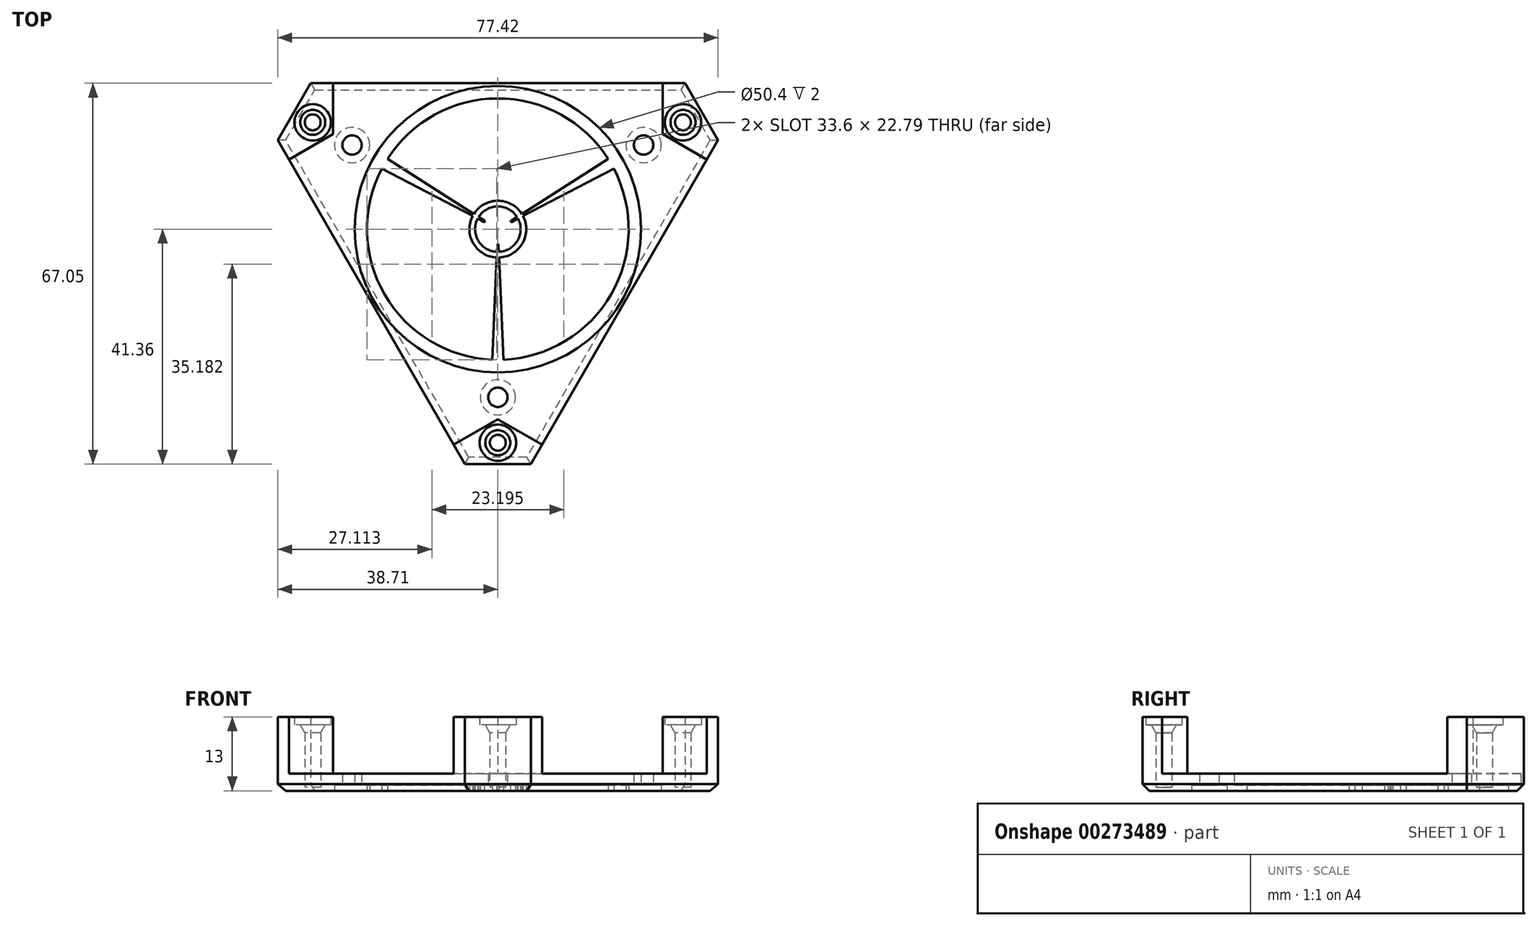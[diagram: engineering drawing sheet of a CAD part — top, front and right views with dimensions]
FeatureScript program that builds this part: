
annotation { "Feature Type Name" : "Feature", "Feature Type Description" : "" }
export const myFeature = defineFeature(function(context is Context, id is Id, definition is map)
    precondition{}
    {
        {
            var Q0;
            Q0=qCreatedBy(makeId("Top.planeOp"),FACE);
            var sketch = newSketch(context, id + "F0", { "sketchPlane" : qUnion([Q0])});
            skLineSegment(sketch, "E0", {"start": v(0, 0) * mm, "end": v(0, 47) * mm, "construction": true});
            skLineSegment(sketch, "E1", {"start": v(0, 47) * mm, "end": v(15, 47) * mm, "construction": true});
            skLineSegment(sketch, "E2", {"start": v(0, 0) * mm, "end": v(0, -29.6) * mm, "construction": true});
            skCircle(sketch, "E3", {"center": v(0, -29.6) * mm, "radius": 1.7 * mm});
            skCircle(sketch, "E4", {"center": v(15, 47) * mm, "radius": 1.7 * mm});
            skLineSegment(sketch, "E5", {"start": v(13.3, 47) * mm, "end": v(13.3, 49.47) * mm});
            skLineSegment(sketch, "E6", {"start": v(13.3, 47) * mm, "end": v(13.3, 44.53) * mm});
            skCircle(sketch, "E7", {"center": v(0, -29.6) * mm, "radius": 3.1 * mm});
            skCircle(sketch, "E8", {"center": v(0, 0) * mm, "radius": 4 * mm});
            skCircle(sketch, "E9", {"center": v(0, 0) * mm, "radius": 25.2 * mm});
            skCircle(sketch, "E10", {"center": v(0, 0) * mm, "radius": 23 * mm});
            skCircle(sketch, "E11", {"center": v(0, 0) * mm, "radius": 5 * mm});
            skLineSegment(sketch, "E12", {"start": v(0, -29.6) * mm, "end": v(0, -33.6) * mm, "construction": true});
            skLineSegment(sketch, "E13", {"start": v(0, -33.6) * mm, "end": v(0, 55) * mm, "construction": true});
            skLineSegment(sketch, "E14", {"start": v(0, 55) * mm, "end": v(11, 55) * mm});
            skLineSegment(sketch, "E15.5.0", {"start": v(0, 0) * mm, "end": v(28.5, 16.45) * mm, "construction": true});
            skLineSegment(sketch, "E16", {"start": v(11, 55) * mm, "end": v(28.5, 40.45) * mm});
            skCircle(sketch, "E17", {"center": v(15, 47) * mm, "radius": 3 * mm});
            skLineSegment(sketch, "E18", {"start": v(13.3, 49.47) * mm, "end": v(13.3, 44.53) * mm});
            skCircle(sketch, "E19", {"center": v(0, 0) * mm, "radius": 0.5 * mm});
            skLineSegment(sketch, "E20", {"start": v(0, -0.5) * mm, "end": v(1, -22.98) * mm});
            skLineSegment(sketch, "E21.MirrorCS", {"start": v(0, -0.5) * mm, "end": v(-1, -22.98) * mm});
            skLineSegment(sketch, "E22", {"start": v(28.5, 40.45) * mm, "end": v(28.5, 16.45) * mm});
            skLineSegment(sketch, "E23.MirrorCS", {"start": v(-13.3, 49.47) * mm, "end": v(-13.3, 44.53) * mm});
            skLineSegment(sketch, "E24.MirrorCS", {"start": v(0, 55) * mm, "end": v(-11, 55) * mm});
            skCircle(sketch, "E25.MirrorC", {"center": v(-15, 47) * mm, "radius": 1.7 * mm});
            skCircle(sketch, "E26.MirrorC", {"center": v(-15, 47) * mm, "radius": 3 * mm});
            skLineSegment(sketch, "E27.MirrorCS", {"start": v(-28.5, 40.45) * mm, "end": v(-28.5, 16.45) * mm});
            skLineSegment(sketch, "E28.MirrorCS", {"start": v(-11, 55) * mm, "end": v(-28.5, 40.45) * mm});
            skLineSegment(sketch, "E29.1.0", {"start": v(-42.13, -37.03) * mm, "end": v(-20.78, -44.9) * mm});
            skLineSegment(sketch, "E29.1.1", {"start": v(-36.2, -36.25) * mm, "end": v(-31.91, -33.78) * mm});
            skLineSegment(sketch, "E29.1.2", {"start": v(-47.63, -27.5) * mm, "end": v(-42.13, -37.03) * mm});
            skLineSegment(sketch, "E29.1.3", {"start": v(-20.78, -44.9) * mm, "end": v(0, -32.9) * mm});
            skCircle(sketch, "E29.1.4", {"center": v(-33.2, -36.5) * mm, "radius": 1.7 * mm});
            skCircle(sketch, "E29.1.5", {"center": v(-33.2, -36.5) * mm, "radius": 3 * mm});
            skLineSegment(sketch, "E29.1.6", {"start": v(-47.63, -27.5) * mm, "end": v(-53.13, -17.97) * mm});
            skLineSegment(sketch, "E29.1.7", {"start": v(-53.13, -17.97) * mm, "end": v(-49.28, 4.45) * mm});
            skLineSegment(sketch, "E29.1.8", {"start": v(-49.28, 4.45) * mm, "end": v(-28.5, 16.45) * mm});
            skCircle(sketch, "E29.1.9", {"center": v(-48.2, -10.5) * mm, "radius": 3 * mm});
            skLineSegment(sketch, "E29.1.10", {"start": v(-49.5, -13.22) * mm, "end": v(-45.21, -10.75) * mm});
            skCircle(sketch, "E29.1.11", {"center": v(-48.2, -10.5) * mm, "radius": 1.7 * mm});
            skLineSegment(sketch, "E29.1.12", {"start": v(0.43, 0.25) * mm, "end": v(19.4, 12.36) * mm});
            skLineSegment(sketch, "E29.1.13", {"start": v(0.43, 0.25) * mm, "end": v(20.4, 10.62) * mm});
            skCircle(sketch, "E29.1.14", {"center": v(25.63, 14.8) * mm, "radius": 3.1 * mm});
            skCircle(sketch, "E29.1.15", {"center": v(25.63, 14.8) * mm, "radius": 1.7 * mm});
            skLineSegment(sketch, "E29.2.0", {"start": v(53.13, -17.97) * mm, "end": v(49.28, 4.45) * mm});
            skLineSegment(sketch, "E29.2.1", {"start": v(49.5, -13.22) * mm, "end": v(45.21, -10.75) * mm});
            skLineSegment(sketch, "E29.2.2", {"start": v(47.63, -27.5) * mm, "end": v(53.13, -17.97) * mm});
            skLineSegment(sketch, "E29.2.3", {"start": v(49.28, 4.45) * mm, "end": v(28.5, 16.45) * mm});
            skCircle(sketch, "E29.2.4", {"center": v(48.2, -10.5) * mm, "radius": 1.7 * mm});
            skCircle(sketch, "E29.2.5", {"center": v(48.2, -10.5) * mm, "radius": 3 * mm});
            skLineSegment(sketch, "E29.2.6", {"start": v(47.63, -27.5) * mm, "end": v(42.13, -37.03) * mm});
            skLineSegment(sketch, "E29.2.7", {"start": v(42.13, -37.03) * mm, "end": v(20.78, -44.9) * mm});
            skLineSegment(sketch, "E29.2.8", {"start": v(20.78, -44.9) * mm, "end": v(0, -32.9) * mm});
            skCircle(sketch, "E29.2.9", {"center": v(33.2, -36.5) * mm, "radius": 3 * mm});
            skLineSegment(sketch, "E29.2.10", {"start": v(36.2, -36.25) * mm, "end": v(31.91, -33.78) * mm});
            skCircle(sketch, "E29.2.11", {"center": v(33.2, -36.5) * mm, "radius": 1.7 * mm});
            skLineSegment(sketch, "E29.2.12", {"start": v(-0.43, 0.25) * mm, "end": v(-20.4, 10.62) * mm});
            skLineSegment(sketch, "E29.2.13", {"start": v(-0.43, 0.25) * mm, "end": v(-19.4, 12.36) * mm});
            skCircle(sketch, "E29.2.14", {"center": v(-25.63, 14.8) * mm, "radius": 3.1 * mm});
            skCircle(sketch, "E29.2.15", {"center": v(-25.63, 14.8) * mm, "radius": 1.7 * mm});
            skLineSegment(sketch, "E30", {"start": v(0, -29.6) * mm, "end": v(0, -37.6) * mm, "construction": true});
            skCircle(sketch, "E31", {"center": v(0, -37.6) * mm, "radius": 1.4 * mm});
            skCircle(sketch, "E32", {"center": v(0, -37.6) * mm, "radius": 3.2 * mm});
            skLineSegment(sketch, "E33", {"start": v(8, -37.53) * mm, "end": v(5.8, -41.36) * mm});
            skLineSegment(sketch, "E34", {"start": v(5.8, -41.36) * mm, "end": v(5.8, -41.36) * mm});
            skLineSegment(sketch, "E35.MirrorCS", {"start": v(-8, -37.53) * mm, "end": v(-5.8, -41.36) * mm});
            skLineSegment(sketch, "E36", {"start": v(-5.8, -41.36) * mm, "end": v(5.8, -41.36) * mm});
            skLineSegment(sketch, "E37.1.0", {"start": v(28.5, 25.7) * mm, "end": v(32.92, 25.7) * mm});
            skLineSegment(sketch, "E37.1.1", {"start": v(38.7, 15.66) * mm, "end": v(32.92, 25.7) * mm});
            skLineSegment(sketch, "E37.1.2", {"start": v(36.5, 11.84) * mm, "end": v(38.7, 15.66) * mm});
            skCircle(sketch, "E37.1.3", {"center": v(32.56, 18.8) * mm, "radius": 3.2 * mm});
            skCircle(sketch, "E37.1.4", {"center": v(32.56, 18.8) * mm, "radius": 1.4 * mm});
            skLineSegment(sketch, "E37.2.0", {"start": v(-36.5, 11.84) * mm, "end": v(-38.7, 15.66) * mm});
            skLineSegment(sketch, "E37.2.1", {"start": v(-32.92, 25.7) * mm, "end": v(-38.7, 15.66) * mm});
            skLineSegment(sketch, "E37.2.2", {"start": v(-28.5, 25.7) * mm, "end": v(-32.92, 25.7) * mm});
            skCircle(sketch, "E37.2.3", {"center": v(-32.56, 18.8) * mm, "radius": 3.2 * mm});
            skCircle(sketch, "E37.2.4", {"center": v(-32.56, 18.8) * mm, "radius": 1.4 * mm});
            skLineSegment(sketch, "E38", {"start": v(8, -37.53) * mm, "end": v(36.5, 11.84) * mm});
            skLineSegment(sketch, "E39", {"start": v(-8, -37.53) * mm, "end": v(-36.5, 11.84) * mm});
            skLineSegment(sketch, "E40", {"start": v(-28.5, 25.7) * mm, "end": v(28.5, 25.7) * mm});
            skLineSegment(sketch, "E41", {"start": v(-7.76, -37.95) * mm, "end": v(0, -33.47) * mm});
            skLineSegment(sketch, "E42", {"start": v(0, -33.47) * mm, "end": v(7.76, -37.95) * mm});
            skLineSegment(sketch, "E43.1.0", {"start": v(36.74, 12.25) * mm, "end": v(28.98, 16.73) * mm});
            skLineSegment(sketch, "E43.1.1", {"start": v(28.98, 16.73) * mm, "end": v(28.98, 25.7) * mm});
            skLineSegment(sketch, "E43.2.0", {"start": v(-28.98, 25.7) * mm, "end": v(-28.98, 16.73) * mm});
            skLineSegment(sketch, "E43.2.1", {"start": v(-28.98, 16.73) * mm, "end": v(-36.74, 12.25) * mm});
            skSolve(sketch);
        }
        {
            var Q0;
            Q0=makeQuery(id+"F0.imprint","IMPRINT",FACE,{"disambiguationData":[TD([[makeQuery(id+"F0.imprint","IMPRINT",EDGE,{"derivedFrom":sQuery(id+"F0.wireOp",EDGE,"E7")}),-1.0]])]});
            var Q1;
            Q1=makeQuery(id+"F0.imprint","IMPRINT",FACE,{"disambiguationData":[TD([[makeQuery(id+"F0.imprint","IMPRINT",EDGE,{"derivedFrom":sQuery(id+"F0.wireOp",EDGE,"E29.2.14")}),1.0]])]});
            var Q2;
            Q2=makeQuery(id+"F0.imprint","IMPRINT",FACE,{"disambiguationData":[TD([[makeQuery(id+"F0.imprint","IMPRINT",EDGE,{"derivedFrom":sQuery(id+"F0.wireOp",EDGE,"E29.1.14")}),1.0]])]});
            var Q3;
            Q3=makeQuery(id+"F0.imprint","IMPRINT",FACE,{"disambiguationData":[TD([[makeQuery(id+"F0.imprint","IMPRINT",EDGE,{"derivedFrom":sQuery(id+"F0.wireOp",EDGE,"E3")}),-1.0]])]});
            var Q4;
            {var subQ3=sQuery(id+"F0.wireOp",EDGE,"E43.2.0");Q4=makeQuery(id+"F0.imprint","IMPRINT",FACE,{"disambiguationData":[TD([[makeQuery(id+"F0.imprint","IMPRINT",EDGE,{"derivedFrom":subQ3}),1.0]])]});}
            var Q5;
            {var subQ3=sQuery(id+"F0.wireOp",EDGE,"E43.1.0");Q5=makeQuery(id+"F0.imprint","IMPRINT",FACE,{"disambiguationData":[TD([[makeQuery(id+"F0.imprint","IMPRINT",EDGE,{"derivedFrom":subQ3}),1.0]])]});}
            var Q6;
            {var subQ3=sQuery(id+"F0.wireOp",EDGE,"E41");Q6=makeQuery(id+"F0.imprint","IMPRINT",FACE,{"disambiguationData":[TD([[makeQuery(id+"F0.imprint","IMPRINT",EDGE,{"derivedFrom":subQ3}),1.0]])]});}
            extrude(context, id + "F1", {"entities" : qUnion([Q0, Q1, Q2, Q3, Q4, Q5, Q6]), "offsetDistance" : 25 * mm, "depth" : 3 * mm});
        }
        {
            var Q0;
            {var subQ0=sQuery(id+"F0.wireOp",EDGE,"E20");var subQ1=sQuery(id+"F0.wireOp",EDGE,"E10");var subQ2=makeQuery(id+"F0.imprint","INTERSECT",VERTEX,{"derivedFrom":[subQ1,subQ0]});Q0=makeQuery(id+"F0.imprint","IMPRINT",FACE,{"disambiguationData":[TD([[makeQuery(id+"F0.imprint","IMPRINT",EDGE,{"disambiguationData":[TD([[subQ2,1.0]])],"derivedFrom":subQ1}),1.0]])]});}
            var Q1;
            Q1=makeQuery(id+"F0.imprint","IMPRINT",FACE,{"disambiguationData":[TD([[makeQuery(id+"F0.imprint","IMPRINT",EDGE,{"derivedFrom":sQuery(id+"F0.wireOp",EDGE,"E9")}),1.0]])]});
            var Q2;
            {var subQ0=sQuery(id+"F0.wireOp",EDGE,"E29.1.12");var subQ1=sQuery(id+"F0.wireOp",EDGE,"E10");var subQ2=makeQuery(id+"F0.imprint","INTERSECT",VERTEX,{"derivedFrom":[subQ1,subQ0]});Q2=makeQuery(id+"F0.imprint","IMPRINT",FACE,{"disambiguationData":[TD([[makeQuery(id+"F0.imprint","IMPRINT",EDGE,{"disambiguationData":[TD([[subQ2,1.0]])],"derivedFrom":subQ1}),1.0]])]});}
            var Q3;
            {var subQ0=sQuery(id+"F0.wireOp",EDGE,"E29.2.12");var subQ1=sQuery(id+"F0.wireOp",EDGE,"E10");var subQ2=makeQuery(id+"F0.imprint","INTERSECT",VERTEX,{"derivedFrom":[subQ1,subQ0]});Q3=makeQuery(id+"F0.imprint","IMPRINT",FACE,{"disambiguationData":[TD([[makeQuery(id+"F0.imprint","IMPRINT",EDGE,{"disambiguationData":[TD([[subQ2,1.0]])],"derivedFrom":subQ1}),1.0]])]});}
            var Q4;
            {var subQ0=sQuery(id+"F0.wireOp",EDGE,"E29.2.12");var subQ1=sQuery(id+"F0.wireOp",EDGE,"E8");var subQ2=makeQuery(id+"F0.imprint","INTERSECT",VERTEX,{"derivedFrom":[subQ1,subQ0]});Q4=makeQuery(id+"F0.imprint","IMPRINT",FACE,{"disambiguationData":[TD([[makeQuery(id+"F0.imprint","IMPRINT",EDGE,{"disambiguationData":[TD([[subQ2,-1.0]])],"derivedFrom":subQ1}),-1.0]])]});}
            var Q5;
            {var subQ0=sQuery(id+"F0.wireOp",EDGE,"E29.1.13");var subQ1=sQuery(id+"F0.wireOp",EDGE,"E8");var subQ2=makeQuery(id+"F0.imprint","INTERSECT",VERTEX,{"derivedFrom":[subQ1,subQ0]});Q5=makeQuery(id+"F0.imprint","IMPRINT",FACE,{"disambiguationData":[TD([[makeQuery(id+"F0.imprint","IMPRINT",EDGE,{"disambiguationData":[TD([[subQ2,1.0]])],"derivedFrom":subQ1}),-1.0]])]});}
            var Q6;
            {var subQ0=sQuery(id+"F0.wireOp",EDGE,"E21.MirrorCS");var subQ1=sQuery(id+"F0.wireOp",EDGE,"E8");var subQ2=makeQuery(id+"F0.imprint","INTERSECT",VERTEX,{"derivedFrom":[subQ1,subQ0]});Q6=makeQuery(id+"F0.imprint","IMPRINT",FACE,{"disambiguationData":[TD([[makeQuery(id+"F0.imprint","IMPRINT",EDGE,{"disambiguationData":[TD([[subQ2,-1.0]])],"derivedFrom":subQ1}),-1.0]])]});}
            var Q7;
            {var subQ0=sQuery(id+"F0.wireOp",EDGE,"E29.1.12");var subQ1=sQuery(id+"F0.wireOp",EDGE,"E8");var subQ2=makeQuery(id+"F0.imprint","INTERSECT",VERTEX,{"derivedFrom":[subQ1,subQ0]});Q7=makeQuery(id+"F0.imprint","IMPRINT",FACE,{"disambiguationData":[TD([[makeQuery(id+"F0.imprint","IMPRINT",EDGE,{"disambiguationData":[TD([[subQ2,1.0]])],"derivedFrom":subQ1}),-1.0]])]});}
            var Q8;
            {var subQ0=sQuery(id+"F0.wireOp",EDGE,"E29.1.12");var subQ1=sQuery(id+"F0.wireOp",EDGE,"E8");var subQ2=makeQuery(id+"F0.imprint","INTERSECT",VERTEX,{"derivedFrom":[subQ1,subQ0]});Q8=makeQuery(id+"F0.imprint","IMPRINT",FACE,{"disambiguationData":[TD([[makeQuery(id+"F0.imprint","IMPRINT",EDGE,{"disambiguationData":[TD([[subQ2,-1.0]])],"derivedFrom":subQ1}),-1.0]])]});}
            var Q9;
            {var subQ0=sQuery(id+"F0.wireOp",EDGE,"E29.2.13");var subQ1=sQuery(id+"F0.wireOp",EDGE,"E8");var subQ2=makeQuery(id+"F0.imprint","INTERSECT",VERTEX,{"derivedFrom":[subQ1,subQ0]});Q9=makeQuery(id+"F0.imprint","IMPRINT",FACE,{"disambiguationData":[TD([[makeQuery(id+"F0.imprint","IMPRINT",EDGE,{"disambiguationData":[TD([[subQ2,-1.0]])],"derivedFrom":subQ1}),-1.0]])]});}
            var Q10;
            {var subQ0=sQuery(id+"F0.wireOp",EDGE,"E29.1.12");var subQ1=sQuery(id+"F0.wireOp",EDGE,"E8");var subQ2=makeQuery(id+"F0.imprint","INTERSECT",VERTEX,{"derivedFrom":[subQ1,subQ0]});Q10=makeQuery(id+"F0.imprint","IMPRINT",FACE,{"disambiguationData":[TD([[makeQuery(id+"F0.imprint","IMPRINT",EDGE,{"disambiguationData":[TD([[subQ2,1.0]])],"derivedFrom":subQ1}),1.0]])]});}
            var Q11;
            {var subQ0=sQuery(id+"F0.wireOp",EDGE,"E29.2.13");var subQ1=sQuery(id+"F0.wireOp",EDGE,"E8");var subQ2=makeQuery(id+"F0.imprint","INTERSECT",VERTEX,{"derivedFrom":[subQ1,subQ0]});Q11=makeQuery(id+"F0.imprint","IMPRINT",FACE,{"disambiguationData":[TD([[makeQuery(id+"F0.imprint","IMPRINT",EDGE,{"disambiguationData":[TD([[subQ2,-1.0]])],"derivedFrom":subQ1}),1.0]])]});}
            var Q12;
            {var subQ0=sQuery(id+"F0.wireOp",EDGE,"E21.MirrorCS");var subQ1=sQuery(id+"F0.wireOp",EDGE,"E8");var subQ2=makeQuery(id+"F0.imprint","INTERSECT",VERTEX,{"derivedFrom":[subQ1,subQ0]});Q12=makeQuery(id+"F0.imprint","IMPRINT",FACE,{"disambiguationData":[TD([[makeQuery(id+"F0.imprint","IMPRINT",EDGE,{"disambiguationData":[TD([[subQ2,-1.0]])],"derivedFrom":subQ1}),1.0]])]});}
            extrude(context, id + "F2", {"entities" : qUnion([Q0, Q1, Q2, Q3, Q4, Q5, Q6, Q7, Q8, Q9, Q10, Q11, Q12]), "operationType" : NewBodyOperationType.ADD, "depth" : 1 * mm});
        }
        {
            var Q0;
            {var subQ1=sQuery(id+"F0.wireOp",EDGE,"E37.2.1");Q0=makeQuery(id+"F0.imprint","IMPRINT",FACE,{"disambiguationData":[TD([[makeQuery(id+"F0.imprint","IMPRINT",EDGE,{"derivedFrom":subQ1}),1.0]])]});}
            var Q1;
            Q1=makeQuery(id+"F0.imprint","IMPRINT",FACE,{"disambiguationData":[TD([[makeQuery(id+"F0.imprint","IMPRINT",EDGE,{"derivedFrom":sQuery(id+"F0.wireOp",EDGE,"E32")}),-1.0]])]});
            var Q2;
            {var subQ1=sQuery(id+"F0.wireOp",EDGE,"E37.1.1");Q2=makeQuery(id+"F0.imprint","IMPRINT",FACE,{"disambiguationData":[TD([[makeQuery(id+"F0.imprint","IMPRINT",EDGE,{"derivedFrom":subQ1}),1.0]])]});}
            extrude(context, id + "F3", {"entities" : qUnion([Q0, Q1, Q2]), "operationType" : NewBodyOperationType.ADD, "depth" : (3 + 10) * mm});
        }
        {
            var Q0;
            Q0=makeQuery(id+"F0.imprint","IMPRINT",FACE,{"disambiguationData":[TD([[makeQuery(id+"F0.imprint","IMPRINT",EDGE,{"derivedFrom":sQuery(id+"F0.wireOp",EDGE,"E31")}),-1.0]])]});
            var Q1;
            Q1=makeQuery(id+"F0.imprint","IMPRINT",FACE,{"disambiguationData":[TD([[makeQuery(id+"F0.imprint","IMPRINT",EDGE,{"derivedFrom":sQuery(id+"F0.wireOp",EDGE,"E37.2.3")}),1.0]])]});
            var Q2;
            Q2=makeQuery(id+"F0.imprint","IMPRINT",FACE,{"disambiguationData":[TD([[makeQuery(id+"F0.imprint","IMPRINT",EDGE,{"derivedFrom":sQuery(id+"F0.wireOp",EDGE,"E37.1.3")}),1.0]])]});
            extrude(context, id + "F4", {"entities" : qUnion([Q0, Q1, Q2]), "operationType" : NewBodyOperationType.ADD, "depth" : (3 + 9.6 - 1) * mm});
        }
        {
            var Q0;
            Q0=makeQuery(id+"F0.imprint","IMPRINT",FACE,{"disambiguationData":[TD([[makeQuery(id+"F0.imprint","IMPRINT",EDGE,{"derivedFrom":sQuery(id+"F0.wireOp",EDGE,"E31")}),1.0]])]});
            var Q1;
            Q1=makeQuery(id+"F0.imprint","IMPRINT",FACE,{"disambiguationData":[TD([[makeQuery(id+"F0.imprint","IMPRINT",EDGE,{"derivedFrom":sQuery(id+"F0.wireOp",EDGE,"E37.2.4")}),1.0]])]});
            var Q2;
            Q2=makeQuery(id+"F0.imprint","IMPRINT",FACE,{"disambiguationData":[TD([[makeQuery(id+"F0.imprint","IMPRINT",EDGE,{"derivedFrom":sQuery(id+"F0.wireOp",EDGE,"E37.1.4")}),1.0]])]});
            extrude(context, id + "F5", {"entities" : qUnion([Q0, Q1, Q2]), "operationType" : NewBodyOperationType.ADD, "depth" : 0.6 * mm});
        }
        {
            var Q0;
            Q0=makeQuery(id+"F0.imprint","IMPRINT",FACE,{"disambiguationData":[TD([[makeQuery(id+"F0.imprint","IMPRINT",EDGE,{"derivedFrom":sQuery(id+"F0.wireOp",EDGE,"E29.1.14")}),1.0]])]});
            var Q1;
            Q1=makeQuery(id+"F0.imprint","IMPRINT",FACE,{"disambiguationData":[TD([[makeQuery(id+"F0.imprint","IMPRINT",EDGE,{"derivedFrom":sQuery(id+"F0.wireOp",EDGE,"E29.2.14")}),1.0]])]});
            var Q2;
            Q2=makeQuery(id+"F0.imprint","IMPRINT",FACE,{"disambiguationData":[TD([[makeQuery(id+"F0.imprint","IMPRINT",EDGE,{"derivedFrom":sQuery(id+"F0.wireOp",EDGE,"E3")}),-1.0]])]});
            extrude(context, id + "F6", {"entities" : qUnion([Q0, Q1, Q2]), "operationType" : NewBodyOperationType.REMOVE, "depth" : 1 * mm});
        }
        {
            var Q0;
            Q0=makeQuery(id+"F4.opExtrude","CAP_EDGE",EDGE,{"disambiguationData":[OSD([sQuery(id+"F0.wireOp",EDGE,"E37.2.4")])],"isStart":false});
            var Q1;
            Q1=makeQuery(id+"F4.opExtrude","CAP_EDGE",EDGE,{"disambiguationData":[OSD([sQuery(id+"F0.wireOp",EDGE,"E37.1.4")])],"isStart":false});
            var Q2;
            Q2=makeQuery(id+"F4.opExtrude","CAP_EDGE",EDGE,{"disambiguationData":[OSD([sQuery(id+"F0.wireOp",EDGE,"E31")])],"isStart":false});
            chamfer(context, id + "F7", {"entities" : qUnion([Q0, Q1, Q2]), "chamferType" : ChamferType.TWO_OFFSETS, "width1" : 1.4 * mm, "oppositeDirection" : false, "width2" : 0.8 * mm, "tangentPropagation" : true});
        }
        {
            var Q0;
            Q0=makeQuery(id+"F2.opExtrude","SWEPT_EDGE",EDGE,{"disambiguationData":[OSD([sQuery(id+"F0.wireOp",EDGE,"E19"),sQuery(id+"F0.wireOp",EDGE,"E29.2.12"),sQuery(id+"F0.wireOp",EDGE,"E29.2.13")])]});
            var Q1;
            Q1=makeQuery(id+"F2.opExtrude","SWEPT_EDGE",EDGE,{"disambiguationData":[OSD([sQuery(id+"F0.wireOp",EDGE,"E19"),sQuery(id+"F0.wireOp",EDGE,"E29.1.12"),sQuery(id+"F0.wireOp",EDGE,"E29.1.13")])]});
            var Q2;
            Q2=makeQuery(id+"F2.opExtrude","SWEPT_EDGE",EDGE,{"disambiguationData":[OSD([sQuery(id+"F0.wireOp",EDGE,"E19"),sQuery(id+"F0.wireOp",EDGE,"E20"),sQuery(id+"F0.wireOp",EDGE,"E21.MirrorCS")])]});
            fillet(context, id + "F8", {"entities" : qUnion([Q0, Q1, Q2]), "radius" : 0.1 * mm, "tangentPropagation" : true, "allowEdgeOverflow" : false});
        }
        {
            var Q0;
            {var subQ0=sQuery(id+"F0.wireOp",EDGE,"E37.2.0");var subQ1=sQuery(id+"F0.wireOp",EDGE,"E35.MirrorCS");Q0=makeQuery(id+"F3.boolean.opBoolean","MERGE",EDGE,{"derivedFrom":[makeQuery(id+"F1.opExtrude","CAP_EDGE",EDGE,{"disambiguationData":[OSD([subQ1,subQ0,sQuery(id+"F0.wireOp",EDGE,"E39")])],"isStart":true}),makeQuery(id+"F3.opExtrude","CAP_EDGE",EDGE,{"disambiguationData":[OSD([subQ1])],"isStart":true}),makeQuery(id+"F3.opExtrude","CAP_EDGE",EDGE,{"disambiguationData":[OSD([subQ0])],"isStart":true})]});}
            var Q1;
            Q1=makeQuery(id+"F3.opExtrude","CAP_EDGE",EDGE,{"disambiguationData":[OSD([sQuery(id+"F0.wireOp",EDGE,"E37.2.1")])],"isStart":true});
            var Q2;
            {var subQ0=sQuery(id+"F0.wireOp",EDGE,"E37.2.2");var subQ1=sQuery(id+"F0.wireOp",EDGE,"E37.1.0");Q2=makeQuery(id+"F3.boolean.opBoolean","MERGE",EDGE,{"derivedFrom":[makeQuery(id+"F1.opExtrude","CAP_EDGE",EDGE,{"disambiguationData":[OSD([subQ1,subQ0,sQuery(id+"F0.wireOp",EDGE,"E40")])],"isStart":true}),makeQuery(id+"F3.opExtrude","CAP_EDGE",EDGE,{"disambiguationData":[OSD([subQ1])],"isStart":true}),makeQuery(id+"F3.opExtrude","CAP_EDGE",EDGE,{"disambiguationData":[OSD([subQ0])],"isStart":true})]});}
            var Q3;
            Q3=makeQuery(id+"F3.opExtrude","CAP_EDGE",EDGE,{"disambiguationData":[OSD([sQuery(id+"F0.wireOp",EDGE,"E37.1.1")])],"isStart":true});
            var Q4;
            {var subQ0=sQuery(id+"F0.wireOp",EDGE,"E37.1.2");var subQ1=sQuery(id+"F0.wireOp",EDGE,"E33");Q4=makeQuery(id+"F3.boolean.opBoolean","MERGE",EDGE,{"derivedFrom":[makeQuery(id+"F1.opExtrude","CAP_EDGE",EDGE,{"disambiguationData":[OSD([subQ1,subQ0,sQuery(id+"F0.wireOp",EDGE,"E38")])],"isStart":true}),makeQuery(id+"F3.opExtrude","CAP_EDGE",EDGE,{"disambiguationData":[OSD([subQ1])],"isStart":true}),makeQuery(id+"F3.opExtrude","CAP_EDGE",EDGE,{"disambiguationData":[OSD([subQ0])],"isStart":true})]});}
            var Q5;
            Q5=makeQuery(id+"F3.opExtrude","CAP_EDGE",EDGE,{"disambiguationData":[OSD([sQuery(id+"F0.wireOp",EDGE,"E36")])],"isStart":true});
            chamfer(context, id + "F9", {"entities" : qUnion([Q0, Q1, Q2, Q3, Q4, Q5]), "width" : 1.2 * mm, "tangentPropagation" : true});
        }
    });
